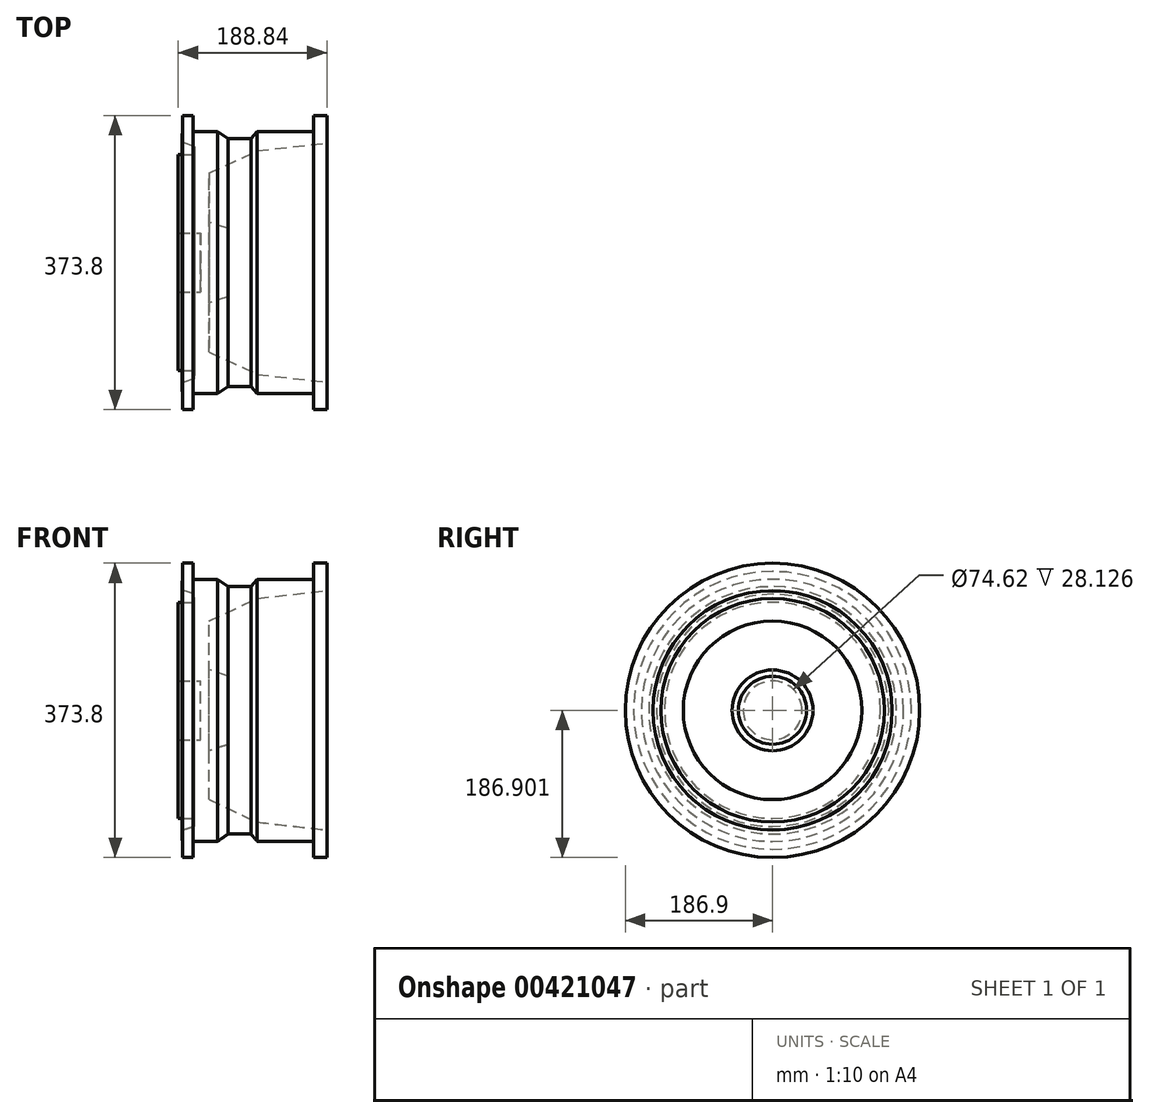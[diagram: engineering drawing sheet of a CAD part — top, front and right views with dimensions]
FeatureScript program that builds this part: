
annotation { "Feature Type Name" : "Feature", "Feature Type Description" : "" }
export const myFeature = defineFeature(function(context is Context, id is Id, definition is map)
    precondition{}
    {
        {
            var Q0;
            Q0=qCreatedBy(makeId("Front.planeOp"),FACE);
            var sketch = newSketch(context, id + "F0", { "sketchPlane" : qUnion([Q0])});
            skLineSegment(sketch, "E0", {"start": v(-76.66, 65.14) * mm, "end": v(-63.25, 65.14) * mm});
            skLineSegment(sketch, "E1", {"start": v(-63.25, 65.14) * mm, "end": v(-63.25, 44.74) * mm});
            skLineSegment(sketch, "E2", {"start": v(-76.66, 65.14) * mm, "end": v(-76.66, 54.65) * mm});
            skLineSegment(sketch, "E3", {"start": v(-63.25, 44.74) * mm, "end": v(-32.06, 44.74) * mm});
            skLineSegment(sketch, "E4", {"start": v(106.68, 30.17) * mm, "end": v(18.07, 20.26) * mm});
            skLineSegment(sketch, "E5", {"start": v(18.07, 20.26) * mm, "end": v(-42.85, -8.3) * mm});
            skLineSegment(sketch, "E6", {"start": v(-42.85, -8.3) * mm, "end": v(-42.85, -70.4) * mm});
            skLineSegment(sketch, "E7", {"start": v(-42.85, -70.4) * mm, "end": v(-18.07, -78.55) * mm});
            skLineSegment(sketch, "E8", {"start": v(-18.07, -78.55) * mm, "end": v(-18.07, -121.76) * mm});
            skLineSegment(sketch, "E9", {"start": v(-18.07, -121.76) * mm, "end": v(-53.92, -121.76) * mm});
            skLineSegment(sketch, "E10", {"start": v(-53.92, -121.76) * mm, "end": v(-53.92, -84.45) * mm});
            skLineSegment(sketch, "E11", {"start": v(-53.92, -84.45) * mm, "end": v(-82.04, -84.45) * mm});
            skLineSegment(sketch, "E12", {"start": v(-82.04, -84.45) * mm, "end": v(-82.04, 15.43) * mm});
            skLineSegment(sketch, "E13", {"start": v(-82.04, 15.43) * mm, "end": v(-61.38, 15.43) * mm});
            skLineSegment(sketch, "E14", {"start": v(-61.38, 15.43) * mm, "end": v(-61.38, 25.76) * mm});
            skLineSegment(sketch, "E15", {"start": v(-61.38, 25.76) * mm, "end": v(-77.07, 30.93) * mm});
            skLineSegment(sketch, "E16", {"start": v(-77.07, 30.93) * mm, "end": v(-76.66, 54.65) * mm});
            skLineSegment(sketch, "E17", {"start": v(-32.06, 44.74) * mm, "end": v(-18.9, 35.52) * mm});
            skLineSegment(sketch, "E18", {"start": v(-18.9, 35.52) * mm, "end": v(10.37, 35.52) * mm});
            skLineSegment(sketch, "E19", {"start": v(10.37, 35.52) * mm, "end": v(18.4, 44.74) * mm});
            skLineSegment(sketch, "E20", {"start": v(18.4, 44.74) * mm, "end": v(90.15, 44.74) * mm});
            skLineSegment(sketch, "E21", {"start": v(90.15, 44.74) * mm, "end": v(90.15, 65.14) * mm});
            skLineSegment(sketch, "E22", {"start": v(90.15, 65.14) * mm, "end": v(106.8, 65.14) * mm});
            skLineSegment(sketch, "E23", {"start": v(106.8, 65.14) * mm, "end": v(106.68, 30.17) * mm});
            skSolve(sketch);
        }
        {
            var Q0;
            Q0 = qSketchRegion(id + "F0", true);
            var Q1;
            Q1=sQuery(id+"F0.wireOp",EDGE,"E9");
            revolve(context, id + "F1", {"entities" : qUnion([Q0]), "axis" : qUnion([Q1]), "revolveType" : RevolveType.FULL});
        }
    });
